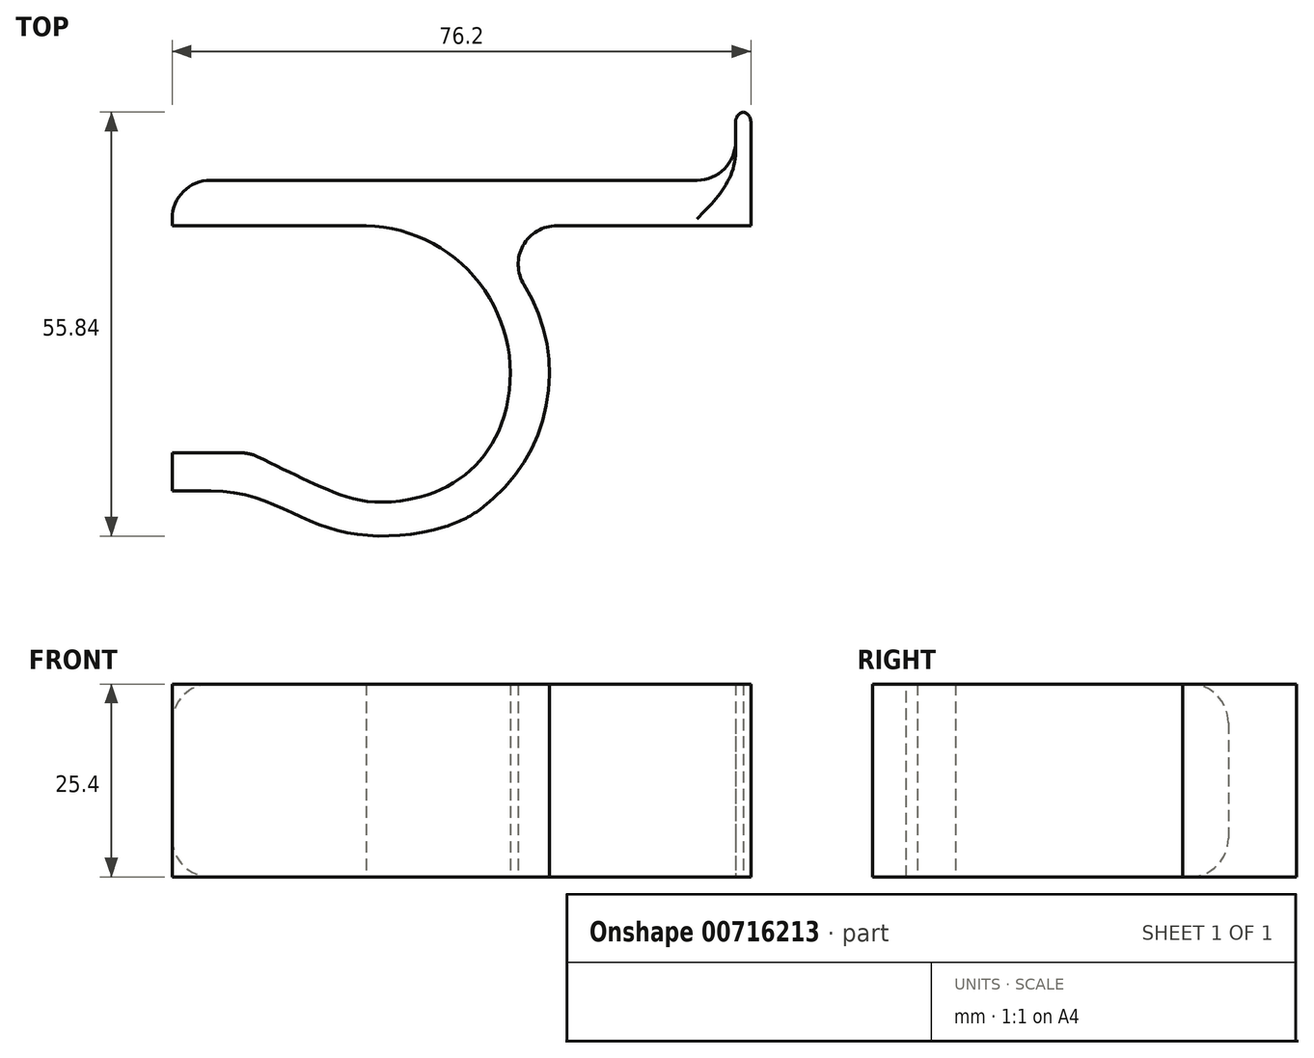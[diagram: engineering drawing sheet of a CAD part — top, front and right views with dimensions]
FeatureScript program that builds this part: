
annotation { "Feature Type Name" : "Feature", "Feature Type Description" : "" }
export const myFeature = defineFeature(function(context is Context, id is Id, definition is map)
    precondition{}
    {
        {
            var Q0;
            Q0=qCreatedBy(makeId("Top.planeOp"),FACE);
            var sketch = newSketch(context, id + "F0", { "sketchPlane" : qUnion([Q0])});
            skLineSegment(sketch, "E0.bottom", {"start": v(0, 0) * mm, "end": v(76.2, 0) * mm});
            skLineSegment(sketch, "E0.top", {"start": v(0, 6) * mm, "end": v(74.2, 6) * mm});
            skLineSegment(sketch, "E0.left", {"start": v(0, 0) * mm, "end": v(0, 6) * mm});
            skLineSegment(sketch, "E1.top", {"start": v(74.2, 15) * mm, "end": v(76.2, 15) * mm});
            skLineSegment(sketch, "E1.left", {"start": v(74.2, 6) * mm, "end": v(74.2, 15) * mm});
            skLineSegment(sketch, "E1.right", {"start": v(76.2, 0) * mm, "end": v(76.2, 15) * mm});
            skLineSegment(sketch, "E2", {"start": v(0, -34.9) * mm, "end": v(5.1, -34.9) * mm});
            skArc(sketch, "E3", {"start": v(38.1, -38.9) * mm, "mid": v(49.68, -19.45) * mm, "end": v(38.1, 0) * mm});
            skPoint(sketch, "E3.startSnap0", {"position": v(38.1, 0) * mm});
            skFitSpline(sketch, "E4", {"points": [v(38.1, -38.9) * mm, v(20.4, -39.74) * mm, v(5.1, -34.9) * mm], "startDerivative": vector(-37.4, -13.94) * mm, "endDerivative": vector(-40.18, 0) * mm});
            skLineSegment(sketch, "E5", {"start": v(0, -34.9) * mm, "end": v(0, -29.9) * mm});
            skLineSegment(sketch, "E6", {"start": v(0, -29.9) * mm, "end": v(10.18, -29.9) * mm});
            skFitSpline(sketch, "E7", {"points": [v(10.18, -29.9) * mm, v(20.4, -34.74) * mm, v(38.1, -33.9) * mm], "startDerivative": vector(22.72, -10.68) * mm, "endDerivative": vector(51.19, 20.4) * mm});
            skArc(sketch, "E8", {"start": v(38.1, -33.9) * mm, "mid": v(43.32, -12.69) * mm, "end": v(25.53, 0) * mm});
            skSolve(sketch);
        }
        {
            var Q0;
            Q0 = qSketchRegion(id + "F0", true);
            extrude(context, id + "F1", {"entities" : qUnion([Q0]), "depth" : 25.4 * mm, "offsetDistance" : 25.4 * mm});
        }
        {
            var Q0;
            Q0=makeQuery(id+"F1.opExtrude","CAP_EDGE",EDGE,{"disambiguationData":[OSD([sQuery(id+"F0.wireOp",EDGE,"E0.top")])],"isStart":false});
            var Q1;
            Q1=makeQuery(id+"F1.opExtrude","CAP_EDGE",EDGE,{"disambiguationData":[OSD([sQuery(id+"F0.wireOp",EDGE,"E0.top")])],"isStart":true});
            fillet(context, id + "F2", {"entities" : qUnion([Q0, Q1]), "radius" : 5.08 * mm, "tangentPropagation" : true, "allowEdgeOverflow" : false});
        }
        {
            var Q0;
            Q0=makeQuery(id+"F1.opExtrude","SWEPT_EDGE",EDGE,{"disambiguationData":[OSD([sQuery(id+"F0.wireOp",EDGE,"E0.top"),sQuery(id+"F0.wireOp",EDGE,"E1.left")])]});
            fillet(context, id + "F3", {"entities" : qUnion([Q0]), "radius" : 5.08 * mm, "tangentPropagation" : true, "allowEdgeOverflow" : false});
        }
        {
            var Q0;
            Q0=makeQuery(id+"F1.opExtrude","SWEPT_EDGE",EDGE,{"disambiguationData":[OSD([sQuery(id+"F0.wireOp",EDGE,"E1.top"),sQuery(id+"F0.wireOp",EDGE,"E1.left")])]});
            var Q1;
            Q1=makeQuery(id+"F1.opExtrude","SWEPT_EDGE",EDGE,{"disambiguationData":[OSD([sQuery(id+"F0.wireOp",EDGE,"E1.top"),sQuery(id+"F0.wireOp",EDGE,"E1.right")])]});
            fillet(context, id + "F4", {"entities" : qUnion([Q0, Q1]), "radius" : 1.27 * mm, "tangentPropagation" : true, "allowEdgeOverflow" : false});
        }
        {
            var Q0;
            Q0=makeQuery(id+"F1.opExtrude","SWEPT_EDGE",EDGE,{"disambiguationData":[OSD([sQuery(id+"F0.wireOp",EDGE,"E3"),sQuery(id+"F0.wireOp",EDGE,"E4")])]});
            var Q1;
            Q1=makeQuery(id+"F1.opExtrude","SWEPT_EDGE",EDGE,{"disambiguationData":[OSD([sQuery(id+"F0.wireOp",EDGE,"E7"),sQuery(id+"F0.wireOp",EDGE,"E8")])]});
            fillet(context, id + "F5", {"entities" : qUnion([Q0, Q1]), "radius" : 15.24 * mm, "tangentPropagation" : true, "allowEdgeOverflow" : false});
        }
        {
            var Q0;
            Q0=makeQuery(id+"F1.opExtrude","SWEPT_EDGE",EDGE,{"disambiguationData":[OSD([sQuery(id+"F0.wireOp",EDGE,"E0.bottom"),sQuery(id+"F0.wireOp",EDGE,"E3")])]});
            fillet(context, id + "F6", {"entities" : qUnion([Q0]), "radius" : 5.08 * mm, "tangentPropagation" : true, "allowEdgeOverflow" : false});
        }
        {
            var Q0;
            Q0=makeQuery(id+"F1.opExtrude","SWEPT_EDGE",EDGE,{"disambiguationData":[OSD([sQuery(id+"F0.wireOp",EDGE,"E6"),sQuery(id+"F0.wireOp",EDGE,"E7")])]});
            fillet(context, id + "F7", {"entities" : qUnion([Q0]), "radius" : 5.08 * mm, "tangentPropagation" : true, "allowEdgeOverflow" : false});
        }
        {
            var Q0;
            Q0=makeQuery(id+"F1.opExtrude","SWEPT_EDGE",EDGE,{"disambiguationData":[OSD([sQuery(id+"F0.wireOp",EDGE,"E0.top"),sQuery(id+"F0.wireOp",EDGE,"E0.left")])]});
            fillet(context, id + "F8", {"entities" : qUnion([Q0]), "radius" : 5.08 * mm, "tangentPropagation" : true, "allowEdgeOverflow" : false});
        }
    });
